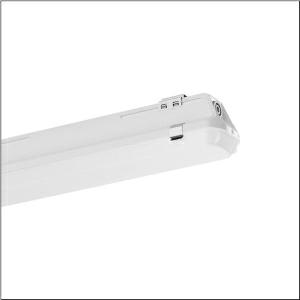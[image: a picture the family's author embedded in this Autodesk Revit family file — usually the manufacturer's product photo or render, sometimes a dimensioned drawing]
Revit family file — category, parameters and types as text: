
# Revit family: monsun_r__21_51fb10mp380b_1725
name_source: partatom
category: Lighting Fixtures
units: mm (PartAtom-declared; Revit-internal decimal feet)

## family parameters
Cut with Voids When Loaded = No
Host = Face
Light Source = No
Part Type = Normal
Room Calculation Point = No
Round Connector Dimension = Use Diameter
Shared = No

## types (1)
- --- (1 x LED, 8190 lm, 59.7 W, 3000K)
    Apparent Load = 60 VA
    CIE Flux Codes = 47 77 93 94 100
    Color Rendering = 80
    Color Temperature = 3000K
    Default Elevation = 1800 mm
    Description = Monsun® 21, damp-proof luminaire, chain hanger, primary optical cover: enclosure, of PMMA, light emission: direct distribution, primary light characteristic: symmetric, installation type: suspended mounting, surface-mounted, horizontal mounting, vertical mounting, LED, rated luminous flux: 8.190lm, luminous efficacy: 153lm/W, light colour: 830, colour temperature: 3000K, control gear: ECG, with terminal, 3-pole, max. 2.5mm², mains connection: 220..240V, AC, 50/60Hz, rated input power: 54W, housing, of glass-fibre reinforced polyester, uncoated, bright grey, incl. chain hanger, length: 1.590mm, width: 90mm, height: 88mm, clip for enclosure, of stainless steel (V2A), ceiling mounting element, of stainless steel (V2A), chain hanger, of stainless steel (V2A), protection rating (complete): IP66, insulation class (complete): insulation class I (protective earthing), certification: CE, ENEC, VDE, UKCA, protection symbol: D, impact resistance: IK04, permissible operating ambient temperature: -25..+35°C, standard: EN 50419, EN 60598-2-1, no direct snow, no direct sun, no direct rain, for indoor or canopied outdoor use, corresponds to IFS (International Featured Standards) requirements for safety and quality in the food industry, contact your sales advisor before using the luminaires in applications with unclear chemical exposure, large temperature fluctuations or condensation-forming humidity, LABS conformity tested according to VDMA 24364:2018-05, packaging unit: 1 piece
    Height = 89 mm
    Lamp = 1 x LED
    Lamp Light Flux = 8190 lm
    Lamp Power = 59.7 W
    Lamp count = 1
    Length = 1590 mm
    Luminous efficacy = 137 lm/W
    Manufacturer = Siteco
    ModVariant = No
    Model = 51FB10MP380B
    Mounting Place = Ceiling
    Mounting Type = Surface mounted
    Number of Poles = 1
    OnlyDefault = Yes
    Power Factor = 1
    Product Name = Monsun® 21
    Product group = damp-proof luminaire
    ProductGroupID = 300
    Protection Class = Protection class I
    Protection Degree = IP 66
    RLX_Detail_Level = 1
    RLX_Emergency_Light_Flux = 0 lm
    RLX_Emergency_Type = 0
    RLX_Emergency_Type_DB = No
    RlxData = <blob elided: 89913 chars, md5=78097a81>
    Socket = socket
    Standby Power = 0 W
    System Light Flux = 8190 lm
    System Power = 60 W
    Type Comments = factory setting: luminous flux: 100 % | (A | C | E) | 134 mA
    Type Image = l_1006717.jpg
    URL = http://relux.com
    VarID = @adj_078905
    Voltage = 0 V
    Weight = 0.00 kg
    Width = 90 mm

## geometry (parser evidence)
native form markers: Blend x4, Sweep x12
no freeform markers — native parametric forms only
